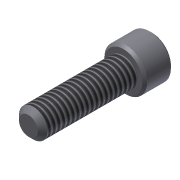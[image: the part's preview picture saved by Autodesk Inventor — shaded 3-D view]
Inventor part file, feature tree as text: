
AUTODESK INVENTOR PART (.ipt)
format: ipt  version: 2011 SP1 (Build 150282100, 282)  size: 109,056 bytes
history: native  units: in
note: dims shown in document units (in); Inventor stores cm internally (conversion verified against a paired STEP export)
features: extrude x3, sketch x3, chamfer x2, thread x1
ambient origin geometry x8: Origin, YZ Plane, XZ Plane, XY Plane, X Axis, Y Axis, Z Axis, Center Point
bodies: Solid1 (feature_tree)
feature tree (9):
  extrude  "Extrusion1"  Depth=0.3937in TaperAngle=0.0deg
  extrude  "Extrusion2"  Depth=0.1181in TaperAngle=0.0deg
  extrude  "Extrusion3"  Depth=0.0591in TaperAngle=0.0deg
  thread  "Thread1"  [1 undecoded]
  chamfer  "Chamfer1"  [1 undecoded]
  chamfer  "Chamfer2"  [1 undecoded]
  sketch  "Sketch1"  dims[d0=0.1181in d1=0.3937in d2=0.0in]
  sketch  "Sketch2"  dims[d3=0.1772in d4=0.1181in d5=0.0in]
  sketch  "Sketch3"  dims[d6=0.0984in d7=0.0591in d8=0.0in d9=0.8661in d10=0.0in d11=0.02in d12=0.125in d13=45.0deg d15=0.0098in d16=0.0787in d17=45.0deg]
note: 3 required parameter values undecoded (feature->parameter linkage not recoverable at this tier; creation-order binding heuristic only, values carry confidence <= 0.55)
